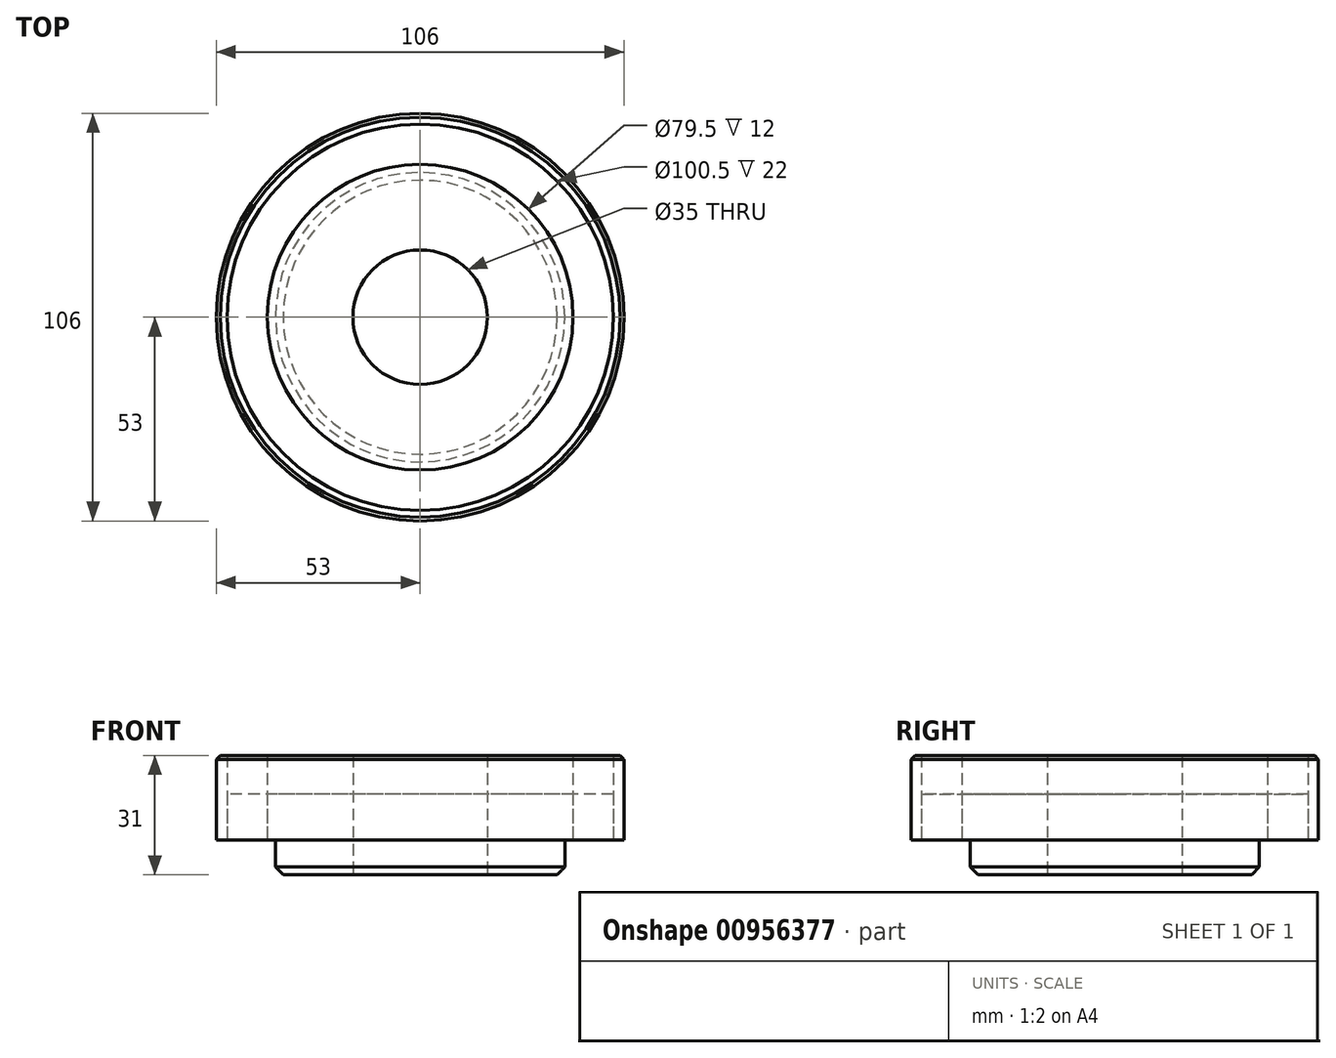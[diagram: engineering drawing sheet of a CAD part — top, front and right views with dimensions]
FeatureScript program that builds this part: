
annotation { "Feature Type Name" : "Feature", "Feature Type Description" : "" }
export const myFeature = defineFeature(function(context is Context, id is Id, definition is map)
    precondition{}
    {
        {
            var Q0;
            Q0=qCreatedBy(makeId("Top.planeOp"),FACE);
            var sketch = newSketch(context, id + "F0", { "sketchPlane" : qUnion([Q0])});
            skCircle(sketch, "E0", {"center": v(0, 0) * mm, "radius": 53 * mm});
            skCircle(sketch, "E1", {"center": v(0, 0) * mm, "radius": 17.5 * mm});
            skCircle(sketch, "E2", {"center": v(0, 0) * mm, "radius": 50.25 * mm});
            skCircle(sketch, "E3", {"center": v(0, 0) * mm, "radius": 39.75 * mm});
            skSolve(sketch);
        }
        {
            var Q0;
            Q0=makeQuery(id+"F0.imprint","IMPRINT",FACE,{"disambiguationData":[TD([[makeQuery(id+"F0.imprint","IMPRINT",EDGE,{"derivedFrom":sQuery(id+"F0.wireOp",EDGE,"E0")}),1.0]])]});
            var Q1;
            Q1=makeQuery(id+"F0.imprint","IMPRINT",FACE,{"disambiguationData":[TD([[makeQuery(id+"F0.imprint","IMPRINT",EDGE,{"derivedFrom":sQuery(id+"F0.wireOp",EDGE,"E1")}),-1.0]])]});
            extrude(context, id + "F1", {"entities" : qUnion([Q0, Q1]), "depth" : 22 * mm, "offsetDistance" : 25 * mm});
        }
        {
            var Q0;
            Q0=makeQuery(id+"F1.opExtrude","CAP_EDGE",EDGE,{"disambiguationData":[OSD([sQuery(id+"F0.wireOp",EDGE,"E0")])],"isStart":false});
            chamfer(context, id + "F2", {"entities" : qUnion([Q0]), "width" : 1 * mm, "tangentPropagation" : true});
        }
        {
            var Q0;
            Q0=makeQuery(id+"F0.imprint","IMPRINT",FACE,{"disambiguationData":[TD([[makeQuery(id+"F0.imprint","IMPRINT",EDGE,{"derivedFrom":sQuery(id+"F0.wireOp",EDGE,"E2")}),1.0]])]});
            extrude(context, id + "F3", {"entities" : qUnion([Q0]), "depth" : 12 * mm, "offsetDistance" : 25 * mm});
        }
        {
            var Q0;
            Q0=makeQuery(id+"F0.imprint","IMPRINT",FACE,{"disambiguationData":[TD([[makeQuery(id+"F0.imprint","IMPRINT",EDGE,{"derivedFrom":sQuery(id+"F0.wireOp",EDGE,"E1")}),-1.0]])]});
            var sketch = newSketch(context, id + "F4", { "sketchPlane" : qUnion([Q0])});
            skCircle(sketch, "E4", {"center": v(0, 0) * mm, "radius": 37.62 * mm});
            skCircle(sketch, "E5", {"center": v(0, 0) * mm, "radius": 17.5 * mm});
            skSolve(sketch);
        }
        {
            var Q0;
            Q0 = qSketchRegion(id + "F4", true);
            extrude(context, id + "F5", {"entities" : qUnion([Q0]), "operationType" : NewBodyOperationType.ADD, "oppositeDirection" : true, "depth" : 9 * mm, "offsetDistance" : 25 * mm});
        }
        {
            var Q0;
            Q0=makeQuery(id+"F5.opExtrude","CAP_EDGE",EDGE,{"disambiguationData":[OSD([sQuery(id+"F4.wireOp",EDGE,"E4")])],"isStart":false});
            chamfer(context, id + "F6", {"entities" : qUnion([Q0]), "width" : 2 * mm, "tangentPropagation" : true});
        }
    });
